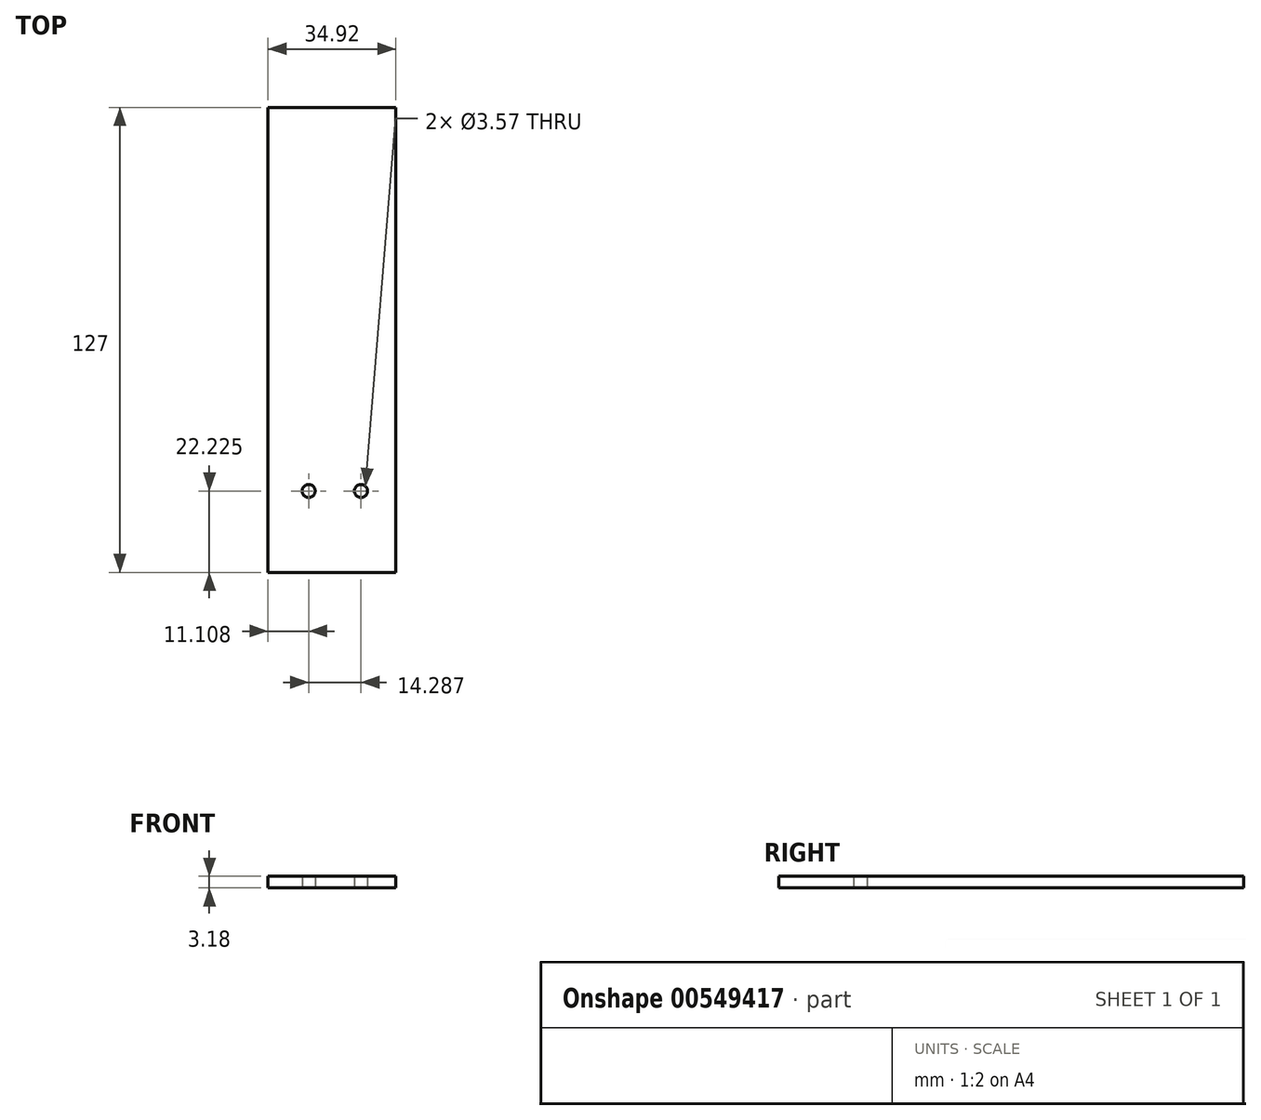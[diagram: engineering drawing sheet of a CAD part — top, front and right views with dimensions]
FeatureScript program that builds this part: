
annotation { "Feature Type Name" : "Feature", "Feature Type Description" : "" }
export const myFeature = defineFeature(function(context is Context, id is Id, definition is map)
    precondition{}
    {
        {
            var Q0;
            Q0=qCreatedBy(makeId("Top.planeOp"),FACE);
            var sketch = newSketch(context, id + "F0", { "sketchPlane" : qUnion([Q0])});
            skLineSegment(sketch, "E0.bottom", {"start": v(-34.92, 63.5) * mm, "end": v(0, 63.5) * mm});
            skLineSegment(sketch, "E0.top", {"start": v(-34.92, -63.5) * mm, "end": v(0, -63.5) * mm});
            skLineSegment(sketch, "E0.left", {"start": v(-34.92, 63.5) * mm, "end": v(-34.92, -63.5) * mm});
            skLineSegment(sketch, "E0.right", {"start": v(0, 63.5) * mm, "end": v(0, -63.5) * mm});
            skCircle(sketch, "E1", {"center": v(-23.81, -41.27) * mm, "radius": 1.79 * mm});
            skCircle(sketch, "E2", {"center": v(-9.53, -41.27) * mm, "radius": 1.79 * mm});
            skSolve(sketch);
        }
        {
            var Q0;
            Q0=makeQuery(id+"F0.imprint","IMPRINT",FACE,{"disambiguationData":[TD([[makeQuery(id+"F0.imprint","IMPRINT",EDGE,{"derivedFrom":sQuery(id+"F0.wireOp",EDGE,"E0.bottom")}),-1.0]])]});
            extrude(context, id + "F1", {"entities" : qUnion([Q0]), "endBound" : BoundingType.SYMMETRIC, "depth" : 3.17 * mm, "offsetDistance" : 25.4 * mm});
        }
    });
